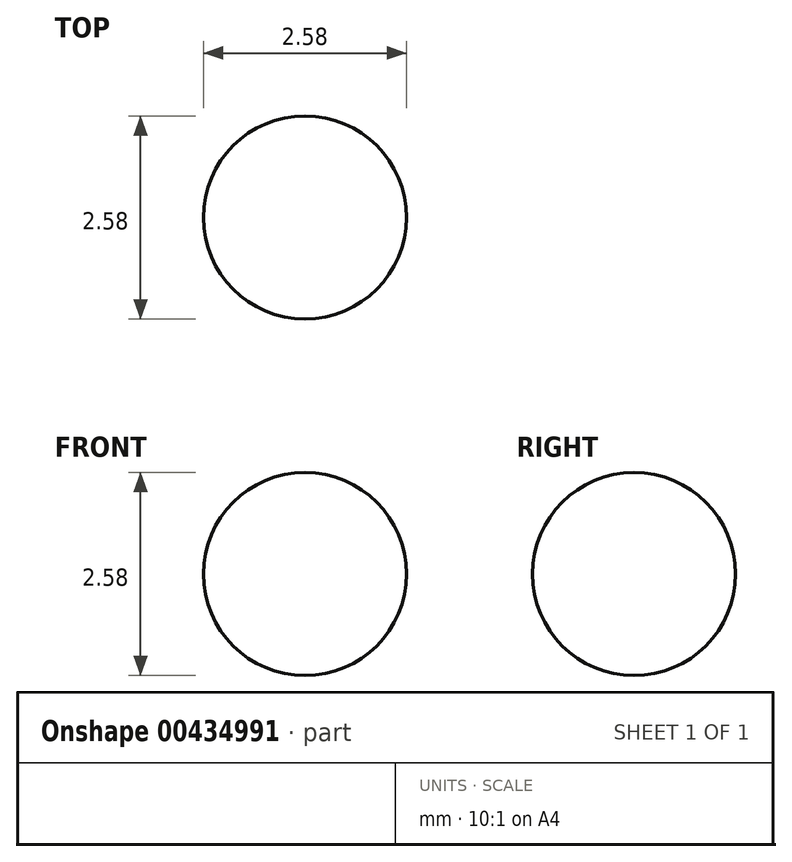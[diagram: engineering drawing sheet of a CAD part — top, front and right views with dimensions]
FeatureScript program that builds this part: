
annotation { "Feature Type Name" : "Feature", "Feature Type Description" : "" }
export const myFeature = defineFeature(function(context is Context, id is Id, definition is map)
    precondition{}
    {
        {
            var Q0;
            Q0=qCreatedBy(makeId("Front.planeOp"),FACE);
            var sketch = newSketch(context, id + "F0", { "sketchPlane" : qUnion([Q0])});
            skLineSegment(sketch, "E0", {"start": v(0, 0) * mm, "end": v(0, 2.58) * mm});
            skArc(sketch, "E1", {"start": v(0, 0) * mm, "mid": v(1.29, 1.29) * mm, "end": v(0, 2.58) * mm});
            skSolve(sketch);
        }
        {
            var Q0;
            Q0 = qSketchRegion(id + "F0", true);
            var Q1;
            Q1=sQuery(id+"F0.wireOp",EDGE,"E0");
            revolve(context, id + "F1", {"entities" : qUnion([Q0]), "axis" : qUnion([Q1]), "revolveType" : RevolveType.FULL});
        }
    });
